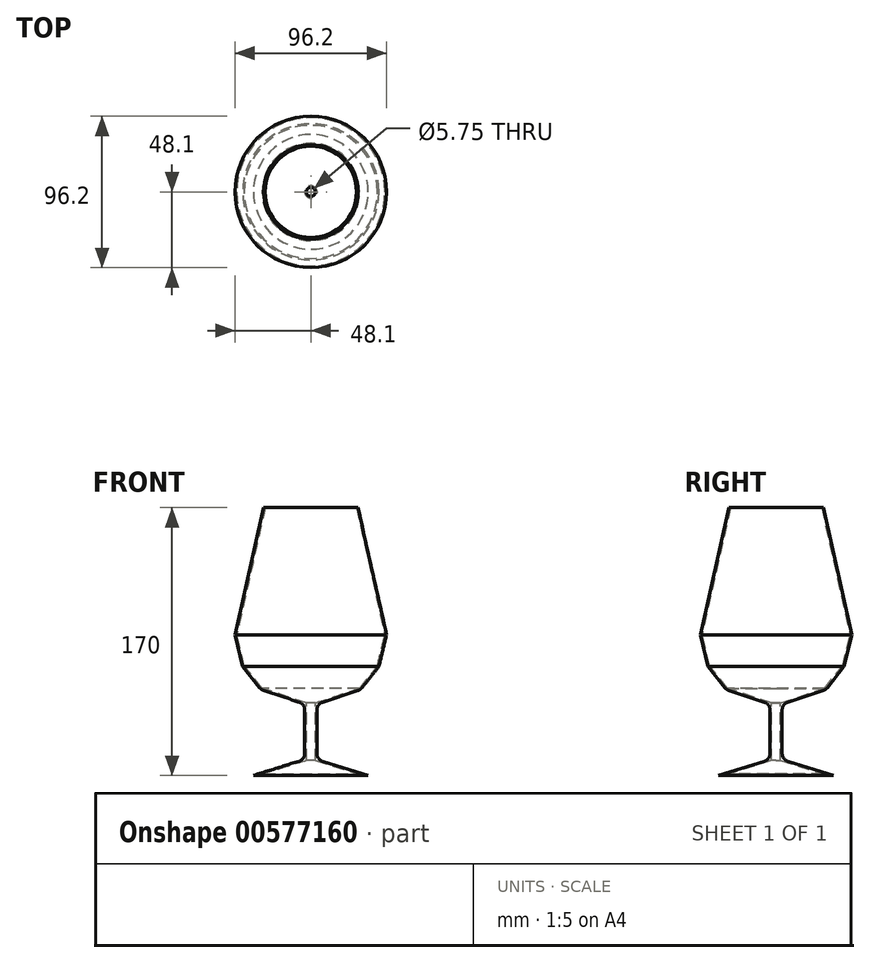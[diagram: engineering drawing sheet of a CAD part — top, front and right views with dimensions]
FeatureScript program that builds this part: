
annotation { "Feature Type Name" : "Feature", "Feature Type Description" : "" }
export const myFeature = defineFeature(function(context is Context, id is Id, definition is map)
    precondition{}
    {
        {
            var Q0;
            Q0=qCreatedBy(makeId("Front.planeOp"),FACE);
            var sketch = newSketch(context, id + "F0", { "sketchPlane" : qUnion([Q0])});
            skLineSegment(sketch, "E0", {"start": v(-30, 100.96) * mm, "end": v(0, 100.96) * mm});
            skLineSegment(sketch, "E1", {"start": v(-30, 100.96) * mm, "end": v(-48.1, 20.29) * mm});
            skLineSegment(sketch, "E2", {"start": v(0, -25.02) * mm, "end": v(-31.52, -14.61) * mm});
            skLineSegment(sketch, "E3", {"start": v(-31.52, -14.61) * mm, "end": v(-43.24, 0) * mm});
            skLineSegment(sketch, "E4", {"start": v(-43.24, 0) * mm, "end": v(-48.1, 20.29) * mm});
            skLineSegment(sketch, "E5", {"start": v(-3.87, -23.74) * mm, "end": v(-3.87, -58.93) * mm});
            skLineSegment(sketch, "E6", {"start": v(-3.87, -58.93) * mm, "end": v(-36.43, -69.04) * mm});
            skLineSegment(sketch, "E7", {"start": v(-36.43, -69.04) * mm, "end": v(0, -69.04) * mm});
            skLineSegment(sketch, "E8", {"start": v(0, 100.96) * mm, "end": v(0, -69.04) * mm});
            skLineSegment(sketch, "E9", {"start": v(0, -69.04) * mm, "end": v(0, -59.04) * mm, "construction": true});
            skSolve(sketch);
        }
        {
            var Q0;
            Q0 = qSketchRegion(id + "F0", true);
            var Q1;
            Q1=sQuery(id+"F0.wireOp",EDGE,"E8");
            revolve(context, id + "F1", {"entities" : qUnion([Q0]), "axis" : qUnion([Q1]), "revolveType" : RevolveType.FULL});
        }
        {
            var Q0;
            Q0=makeQuery(id+"F1.opRevolve","SWEPT_FACE",FACE,{"disambiguationData":[OSD([sQuery(id+"F0.wireOp",EDGE,"E0")])]});
            shell(context, id + "F2", {"entities" : qUnion([Q0]), "thickness" : 1 * mm});
        }
        {
            var Q0;
            Q0=makeQuery(id+"F1.opRevolve","SWEPT_EDGE",EDGE,{"disambiguationData":[OSD([sQuery(id+"F0.wireOp",EDGE,"E5"),sQuery(id+"F0.wireOp",EDGE,"E6")])]});
            var Q1;
            Q1=makeQuery(id+"F1.opRevolve","SWEPT_EDGE",EDGE,{"disambiguationData":[OSD([sQuery(id+"F0.wireOp",EDGE,"E2"),sQuery(id+"F0.wireOp",EDGE,"E5")])]});
            fillet(context, id + "F3", {"entities" : qUnion([Q0, Q1]), "radius" : 5 * mm, "tangentPropagation" : true, "allowEdgeOverflow" : false});
        }
        {
            var Q0;
            Q0=makeQuery(id+"F1.opRevolve","SWEPT_EDGE",EDGE,{"disambiguationData":[OSD([sQuery(id+"F0.wireOp",EDGE,"E2"),sQuery(id+"F0.wireOp",EDGE,"E3")])]});
            fillet(context, id + "F4", {"entities" : qUnion([Q0]), "radius" : 5 * mm, "tangentPropagation" : true, "allowEdgeOverflow" : false});
        }
    });
